# Revit family: SIMES_S.1245W_Streamline
name_source: partatom
category: Lighting Fixtures
revit_build: Autodesk Revit 2016 (Build: 20150714_1515(x64)
units: mm (PartAtom-declared; Revit-internal decimal feet)

## family parameters
Cut with Voids When Loaded = No
Host = Face
Light Source = No
OmniClass Number = 23.80.70.14
OmniClass Title = Luminaries for External Lighting
Part Type = Normal
Room Calculation Point = No
Round Connector Dimension = Use Diameter
Shared = No

## types (1)
- SIMES_S.1245W_Streamline
    Approval mark = CE
    Assembly Code = D5020
    Color Rendering Index = CRI 90
    Colour Temperature = 3000
    Control Gear = electronic transformer
    Default Elevation = 1219 mm
    Description = MINISTREAMLINE PROJECTOR
Art. S.1245W
MODULES LED 3000K  230V CRI 90
Rated luminaire luminous flux: 2310lm
Rated input power: 35W
Luminaire efficacy: 66lm/W
Electronic ballast 220÷240V 50/60Hz
CE

Fixture available with integral DALI driver on request with surcharge.

PRODUCT TYPE
Wall mounted luminaire. IP rating IP 65
MATERIAL CHARACTERISTICS
Die-cast EN AB-47100 aluminium housing with high corrosion resistance. Stone wash surface treatment prior to painting process. A4 grade Stainless Steel screws with 2,5-3% molybdenum content which increases the resistance against corrosion. Pre treated Silicone Gaskets. Painting Process : 3 Step Process
1) Surface treatment with BONDERITE. A heavy metal free chemical surface treatment containing ceramic nano particles giving a cohesive, inorganic and highly dense protective coating. 2) PRE POLYMERIZATION a process of introducing an epoxy primer with excellent characteristics to the paint which also offers very high resistance to oxidation due to its Zinc content. 3) POLYMERIZATION a process with the application of polyester powder with high resistance against UV rays and harsh weather conditions. Resistance test protection for Marine applications for 1200h.  Mechanical resistance IK 07 Maximum load capacity --
LIGHTING PERFORMANCE
Clear toughened glass diffuser. LOR --. Compact electronic ballast to guarantee better lamp stability, lifetime and reduced energy consumption. Projector version: The sophisticated optics focuses the beam and makes the light comfortable by reducing the direct glare of the light source.
INSTALLATION AND MANTEINANCE
Streamline wall mounted allows three different beam settings: 0° - 5° - 10°. Streamline projector suitable with the bracket that allows a 180° product rotation.
WIRING
Luminaire suitable for single cable gland ( projector ) or single grommet ( wall ). Isolation: CLASS I . Available colours: Aluminium grey (cod.14). Weight: 2.3 Kg Glow Wire test: --
Lamp included.
This luminaire contains built-in LED modules with energy class: A, A+, A++. In case of damage or malfunction please contact the manufacturer to receive additional instructions on how to replace and relative spare parts to order. The LED modules cannot be handled in the luminaire by the end user (Regulation UE 874/2012).
LED circuit boards are engineered accordingly to actual Lumen Maintenance regulation (LM80) and Technical Memorandum (TM21) where uniformity and quality of light is 50.000 hours referred to L70  B20 Ta 25°C.Lifecycle refers to LED circuit boards only, all others components of the luminaire are excluded.
    Frequency = 50/60Hz
    IFC Classification = Light Fixture
    IK Rating = IK 07
    Lamp = LED
    Lamp Light Flux = 3300
    Lamp Power = 15,800000190734863
    Lamp count = 1
    Last Update = 08/11/2018 16:39:12
    Lifetime = 50000 L70 B20 Ta 25°C
    Light Output Ratio = 100
    Luminous efficacy = 66
    Manufacturer = SIMES
    Masterformat 2014 Code = 26 56 00
    Masterformat 2014 Description = Exterior Lighting
    Model = S.1245W
    Mounting Place = Ceiling
    Mounting Type = Surface mounted
    NBS Reference Code = 49
    NBS Reference Description = Luminaries And Lamps
    OmniClass Code = 23-35 47 11
    OmniClass Description = Lighting Fixture
    Product Group = projector
    Product Name = Streamline projector
    Protection Class = Protection class I
    Protection Degree = IP 65
    System Light Flux = 2310
    System Power = 35
    Type Comments = SIMES S.p.A. - All rights reserved
    Type Image = ministreamline_proiettore.jpg
    UNSPSC Code = 3911
    URL = http://www.simes.it
    Uniclass 1.4 Code = YJ73
    Uniclass 1.4 Description = Luminaries and lamps
    Uniclass 2.0 Code = PR-49
    Uniclass 2.0 Description = Luminaries and lamps
    Uniclass 2015 Code = EF_70_80
    Uniclass 2015 Name = Lighting
    Uniformat II Code = D5020
    Uniformat II Description = Lighting & Branch Wiring
    Voltage = 220÷240V
    Wattage Comments = 84W

## geometry (parser evidence)
native form markers: Blend x2, Sweep x3
no freeform markers — native parametric forms only
